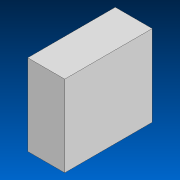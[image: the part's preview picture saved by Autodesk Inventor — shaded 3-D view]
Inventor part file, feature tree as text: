
AUTODESK INVENTOR PART (.ipt)
format: ipt  version: 2022 (Build 260153000, 153)  size: 80,896 bytes
history: native  units: in
note: dims shown in document units (in); Inventor stores cm internally (conversion verified against a paired STEP export)
features: extrude x1, sketch x1
ambient origin geometry x8: Origin, YZ Plane, XZ Plane, XY Plane, X Axis, Y Axis, Z Axis, Center Point
bodies: Solid1 (feature_tree)
feature tree (2):
  extrude  "Extrusion1"  Depth=6.58in
  sketch  "Sketch1"  dims[d0=3.0in d1=6.58in d2=7.1in d3=0.0in]
